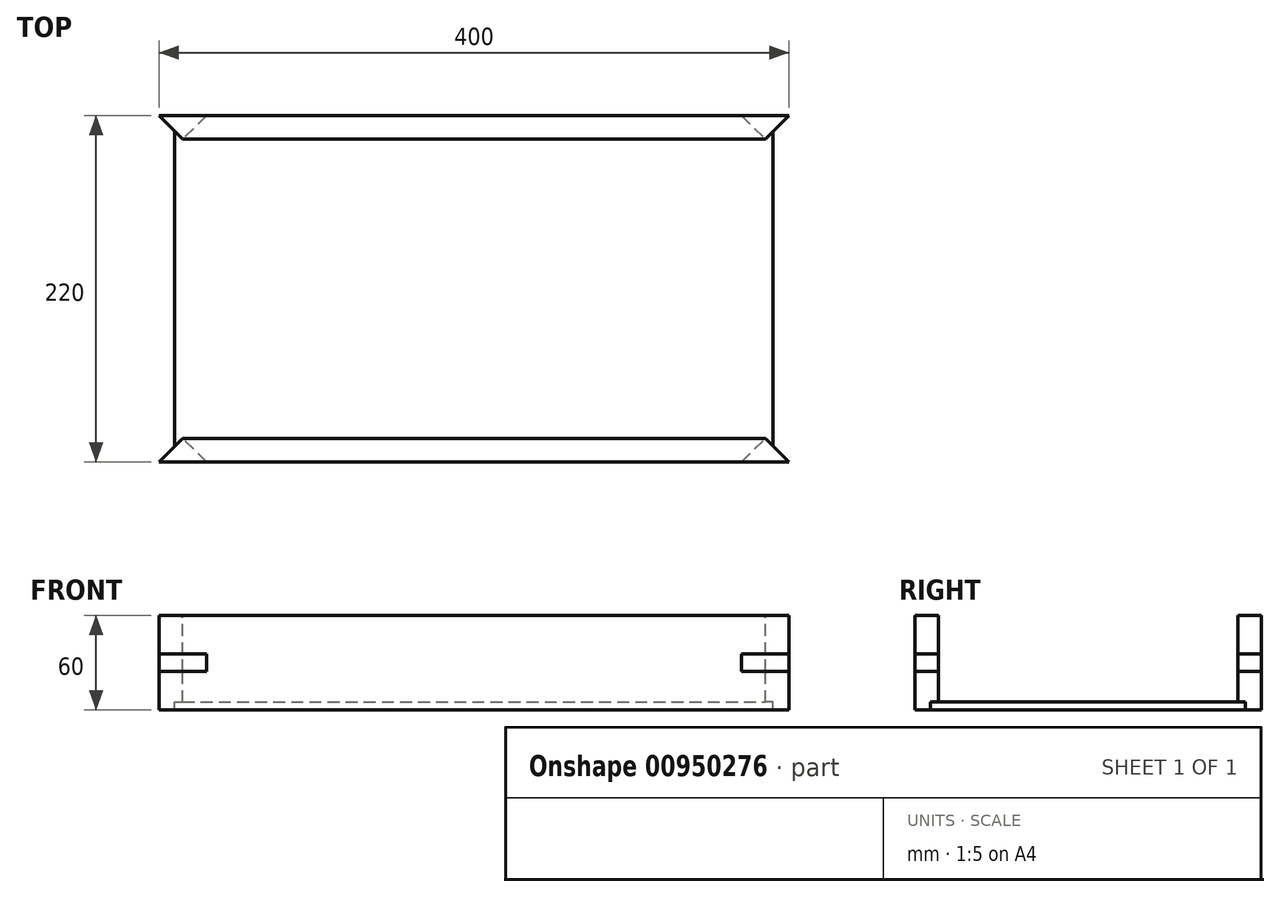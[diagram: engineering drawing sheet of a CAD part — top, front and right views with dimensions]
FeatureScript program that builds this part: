
annotation { "Feature Type Name" : "Feature", "Feature Type Description" : "" }
export const myFeature = defineFeature(function(context is Context, id is Id, definition is map)
    precondition{}
    {
        {
            var Q0;
            Q0=qCreatedBy(makeId("Front.planeOp"),FACE);
            var sketch = newSketch(context, id + "F0", { "sketchPlane" : qUnion([Q0])});
            skLineSegment(sketch, "E0.bottom", {"start": v(200, -30) * mm, "end": v(-200, -30) * mm});
            skLineSegment(sketch, "E0.top", {"start": v(200, 30) * mm, "end": v(-200, 30) * mm});
            skLineSegment(sketch, "E0.left", {"start": v(200, -30) * mm, "end": v(200, 30) * mm});
            skLineSegment(sketch, "E0.right", {"start": v(-200, -30) * mm, "end": v(-200, 30) * mm});
            skPoint(sketch, "E0.middle", {"position": v(0, 0) * mm});
            skSolve(sketch);
        }
        {
            var Q0;
            Q0=makeQuery(id+"F0.imprint","IMPRINT",FACE,{"disambiguationData":[TD([[makeQuery(id+"F0.imprint","IMPRINT",EDGE,{"derivedFrom":sQuery(id+"F0.wireOp",EDGE,"E0.bottom")}),-1.0]])]});
            extrude(context, id + "F1", {"entities" : qUnion([Q0]), "endBound" : BoundingType.SYMMETRIC, "depth" : 15 * mm, "offsetDistance" : 25 * mm});
        }
        {
            var Q0;
            Q0=makeQuery(id+"F1.opExtrude","SWEPT_FACE",FACE,{"disambiguationData":[OSD([sQuery(id+"F0.wireOp",EDGE,"E0.top")])]});
            var sketch = newSketch(context, id + "F2", { "sketchPlane" : qUnion([Q0])});
            skLineSegment(sketch, "E1", {"start": v(200, -7.5) * mm, "end": v(200, 7.5) * mm});
            skLineSegment(sketch, "E2", {"start": v(200, 7.5) * mm, "end": v(185, 7.5) * mm});
            skLineSegment(sketch, "E3", {"start": v(185, 7.5) * mm, "end": v(200, -7.5) * mm});
            skLineSegment(sketch, "E4", {"start": v(-200, -7.5) * mm, "end": v(-200, 7.5) * mm});
            skLineSegment(sketch, "E5", {"start": v(-200, 7.5) * mm, "end": v(-185, 7.5) * mm});
            skLineSegment(sketch, "E6", {"start": v(-185, 7.5) * mm, "end": v(-200, -7.5) * mm});
            skSolve(sketch);
        }
        {
            var Q0;
            Q0=makeQuery(id+"F2.imprint","IMPRINT",FACE,{"disambiguationData":[TD([[makeQuery(id+"F2.imprint","IMPRINT",EDGE,{"derivedFrom":sQuery(id+"F2.wireOp",EDGE,"E4")}),-1.0]])]});
            var Q1;
            Q1=makeQuery(id+"F2.imprint","IMPRINT",FACE,{"disambiguationData":[TD([[makeQuery(id+"F2.imprint","IMPRINT",EDGE,{"derivedFrom":sQuery(id+"F2.wireOp",EDGE,"E1")}),1.0]])]});
            extrude(context, id + "F3", {"entities" : qUnion([Q0, Q1]), "operationType" : NewBodyOperationType.REMOVE, "oppositeDirection" : true, "depth" : 60 * mm, "offsetDistance" : 25 * mm});
        }
        {
            var Q0;
            Q0=makeQuery(id+"F3.boolean.opBoolean","COPY",FACE,{"derivedFrom":makeQuery(id+"F3.opExtrude","SWEPT_FACE",FACE,{"disambiguationData":[OSD([sQuery(id+"F2.wireOp",EDGE,"E3")])]})});
            var sketch = newSketch(context, id + "F4", { "sketchPlane" : qUnion([Q0])});
            skLineSegment(sketch, "E7.bottom", {"start": v(-125.51, -5) * mm, "end": v(-146.72, -5) * mm});
            skLineSegment(sketch, "E7.top", {"start": v(-125.51, 5) * mm, "end": v(-146.72, 5) * mm});
            skLineSegment(sketch, "E7.left", {"start": v(-125.51, -5) * mm, "end": v(-125.51, 5) * mm});
            skLineSegment(sketch, "E7.right", {"start": v(-146.72, -5) * mm, "end": v(-146.72, 5) * mm});
            skPoint(sketch, "E7.middle", {"position": v(-136.12, 0) * mm});
            skSolve(sketch);
        }
        {
            var Q0;
            Q0=makeQuery(id+"F4.imprint","IMPRINT",FACE,{"disambiguationData":[TD([[makeQuery(id+"F4.imprint","IMPRINT",EDGE,{"derivedFrom":sQuery(id+"F4.wireOp",EDGE,"E7.bottom")}),-1.0]])]});
            extrude(context, id + "F5", {"entities" : qUnion([Q0]), "operationType" : NewBodyOperationType.REMOVE, "oppositeDirection" : true, "depth" : 25 * mm, "offsetDistance" : 25 * mm});
        }
        {
            var Q0;
            Q0=makeQuery(id+"F3.boolean.opBoolean","COPY",FACE,{"derivedFrom":makeQuery(id+"F3.opExtrude","SWEPT_FACE",FACE,{"disambiguationData":[OSD([sQuery(id+"F2.wireOp",EDGE,"E6")])]})});
            var sketch = newSketch(context, id + "F6", { "sketchPlane" : qUnion([Q0])});
            skLineSegment(sketch, "E8.bottom", {"start": v(146.72, -5.45) * mm, "end": v(125.51, -5.45) * mm});
            skLineSegment(sketch, "E8.top", {"start": v(146.72, 5.45) * mm, "end": v(125.51, 5.45) * mm});
            skLineSegment(sketch, "E8.left", {"start": v(146.72, -5.45) * mm, "end": v(146.72, 5.45) * mm});
            skLineSegment(sketch, "E8.right", {"start": v(125.51, -5.45) * mm, "end": v(125.51, 5.45) * mm});
            skPoint(sketch, "E8.middle", {"position": v(136.12, 0) * mm});
            skSolve(sketch);
        }
        {
            var Q0;
            Q0=makeQuery(id+"F6.imprint","IMPRINT",FACE,{"disambiguationData":[TD([[makeQuery(id+"F6.imprint","IMPRINT",EDGE,{"derivedFrom":sQuery(id+"F6.wireOp",EDGE,"E8.bottom")}),-1.0]])]});
            extrude(context, id + "F7", {"entities" : qUnion([Q0]), "operationType" : NewBodyOperationType.REMOVE, "oppositeDirection" : true, "depth" : 25 * mm, "offsetDistance" : 25 * mm});
        }
        {
            var Q0;
            Q0=makeQuery(id+"F1.opExtrude","CAP_FACE",FACE,{"disambiguationData":[OSD([sQuery(id+"F0.wireOp",EDGE,"E0.bottom"),sQuery(id+"F0.wireOp",EDGE,"E0.top"),sQuery(id+"F0.wireOp",EDGE,"E0.left"),sQuery(id+"F0.wireOp",EDGE,"E0.right")])],"isStart":false});
            var sketch = newSketch(context, id + "F8", { "sketchPlane" : qUnion([Q0])});
            skLineSegment(sketch, "E9.bottom", {"start": v(160, -25) * mm, "end": v(-160, -25) * mm});
            skLineSegment(sketch, "E9.top", {"start": v(160, 25) * mm, "end": v(-160, 25) * mm});
            skLineSegment(sketch, "E9.left", {"start": v(160, -25) * mm, "end": v(160, 25) * mm});
            skLineSegment(sketch, "E9.right", {"start": v(-160, -25) * mm, "end": v(-160, 25) * mm});
            skPoint(sketch, "E9.middle", {"position": v(0, 0) * mm});
            skSolve(sketch);
        }
        {
            var Q0;
            Q0=makeQuery(id+"F8.imprint","IMPRINT",FACE,{"disambiguationData":[TD([[makeQuery(id+"F8.imprint","IMPRINT",EDGE,{"derivedFrom":sQuery(id+"F8.wireOp",EDGE,"E9.bottom")}),-1.0]])]});
            extrude(context, id + "F9", {"entities" : qUnion([Q0]), "operationType" : NewBodyOperationType.REMOVE, "oppositeDirection" : true, "depth" : 25 * mm, "offsetDistance" : 25 * mm});
        }
        {
            var Q0;
            Q0=makeQuery(id+"F1.opExtrude","CAP_FACE",FACE,{"disambiguationData":[OSD([sQuery(id+"F0.wireOp",EDGE,"E0.bottom"),sQuery(id+"F0.wireOp",EDGE,"E0.top"),sQuery(id+"F0.wireOp",EDGE,"E0.left"),sQuery(id+"F0.wireOp",EDGE,"E0.right")])],"isStart":true});
            var sketch = newSketch(context, id + "F10", { "sketchPlane" : qUnion([Q0])});
            skLineSegment(sketch, "E10.bottom", {"start": v(-160, -25) * mm, "end": v(160, -25) * mm});
            skLineSegment(sketch, "E10.top", {"start": v(-160, -30) * mm, "end": v(160, -30) * mm});
            skLineSegment(sketch, "E10.left", {"start": v(-160, -25) * mm, "end": v(-160, -30) * mm});
            skLineSegment(sketch, "E10.right", {"start": v(160, -25) * mm, "end": v(160, -30) * mm});
            skSolve(sketch);
        }
        {
            var Q0;
            Q0=makeQuery(id+"F10.imprint","IMPRINT",FACE,{"disambiguationData":[TD([[makeQuery(id+"F10.imprint","IMPRINT",EDGE,{"derivedFrom":sQuery(id+"F10.wireOp",EDGE,"E10.bottom")}),-1.0]])]});
            extrude(context, id + "F11", {"entities" : qUnion([Q0]), "operationType" : NewBodyOperationType.REMOVE, "oppositeDirection" : true, "depth" : 5 * mm, "offsetDistance" : 25 * mm});
        }
        {
            var Q0;
            Q0=makeQuery(id+"F11.boolean.opBoolean","MERGE",FACE,{"derivedFrom":[makeQuery(id+"F9.boolean.opBoolean","COPY",FACE,{"derivedFrom":makeQuery(id+"F9.opExtrude","SWEPT_FACE",FACE,{"disambiguationData":[OSD([sQuery(id+"F8.wireOp",EDGE,"E9.right")])]})})],"fromTools":[makeQuery(id+"F11.opExtrude","SWEPT_FACE",FACE,{"disambiguationData":[OSD([sQuery(id+"F10.wireOp",EDGE,"E10.right")])]})]});
            var sketch = newSketch(context, id + "F12", { "sketchPlane" : qUnion([Q0])});
            skLineSegment(sketch, "E11.bottom", {"start": v(7.5, -30) * mm, "end": v(2.5, -30) * mm});
            skLineSegment(sketch, "E11.top", {"start": v(7.5, -25) * mm, "end": v(2.5, -25) * mm});
            skLineSegment(sketch, "E11.left", {"start": v(7.5, -30) * mm, "end": v(7.5, -25) * mm});
            skLineSegment(sketch, "E11.right", {"start": v(2.5, -30) * mm, "end": v(2.5, -25) * mm});
            skSolve(sketch);
        }
        {
            var Q0;
            Q0=makeQuery(id+"F12.imprint","IMPRINT",FACE,{"disambiguationData":[TD([[makeQuery(id+"F12.imprint","IMPRINT",EDGE,{"derivedFrom":sQuery(id+"F12.wireOp",EDGE,"E11.bottom")}),1.0]])]});
            extrude(context, id + "F13", {"entities" : qUnion([Q0]), "operationType" : NewBodyOperationType.REMOVE, "oppositeDirection" : true, "depth" : 50 * mm, "offsetDistance" : 25 * mm});
        }
        {
            var Q0;
            Q0=makeQuery(id+"F1.opExtrude","SWEPT_BODY",BODY,{"disambiguationData":[OSD([sQuery(id+"F0.wireOp",EDGE,"E0.bottom"),sQuery(id+"F0.wireOp",EDGE,"E0.top"),sQuery(id+"F0.wireOp",EDGE,"E0.left"),sQuery(id+"F0.wireOp",EDGE,"E0.right")])]});
            var Q1;
            Q1=qCreatedBy(makeId("Right.planeOp"),FACE);
            mirror(context, id + "F14", {"operationType" : NewBodyOperationType.INTERSECT, "entities" : qUnion([Q0]), "mirrorPlane" : qUnion([Q1])});
        }
        {
            var Q0;
            {var subQ0=makeQuery(id+"F13.boolean.opBoolean","MERGE",FACE,{"derivedFrom":[makeQuery(id+"F11.boolean.opBoolean","COPY",FACE,{"derivedFrom":makeQuery(id+"F11.opExtrude","CAP_FACE",FACE,{"disambiguationData":[OSD([sQuery(id+"F10.wireOp",EDGE,"E10.bottom"),sQuery(id+"F10.wireOp",EDGE,"E10.top"),sQuery(id+"F10.wireOp",EDGE,"E10.left"),sQuery(id+"F10.wireOp",EDGE,"E10.right")])],"isStart":false})})],"fromTools":[makeQuery(id+"F13.opExtrude","SWEPT_FACE",FACE,{"disambiguationData":[OSD([sQuery(id+"F12.wireOp",EDGE,"E11.right")])]})]});Q0=makeQuery(id+"F14.boolean.opBoolean","MERGE",FACE,{"derivedFrom":[subQ0],"fromTools":[makeQuery(id+"F14.boolean.toolComplement.opBoolean","COPY",FACE,{"derivedFrom":makeQuery(id+"F14.opPattern","COPY",FACE,{"derivedFrom":subQ0,"instanceName":"1"})})]});}
            extrude(context, id + "F15", {"entities" : qUnion([Q0]), "depth" : 100 * mm, "offsetDistance" : 25 * mm});
        }
        {
            var Q0;
            Q0=makeQuery(id+"F15.opExtrude","CAP_FACE",FACE,{"disambiguationData":[OSD([sQuery(id+"F10.wireOp",EDGE,"E10.bottom"),sQuery(id+"F10.wireOp",EDGE,"E10.top"),sQuery(id+"F10.wireOp",EDGE,"E10.left"),sQuery(id+"F10.wireOp",EDGE,"E10.right"),sQuery(id+"F12.wireOp",EDGE,"E11.right")])],"isStart":false});
            cPlane(context, id + "F16", {"entities" : qUnion([Q0]), "cplaneType" : CPlaneType.OFFSET, "offset" : 0 * mm, "width" : 150 * mm, "height" : 150 * mm});
        }
        {
            var Q0;
            Q0=makeQuery(id+"F14.boolean.opBoolean","MERGE",FACE,{"derivedFrom":[makeQuery(id+"F5.boolean.opBoolean","COPY",FACE,{"derivedFrom":makeQuery(id+"F5.opExtrude","SWEPT_FACE",FACE,{"disambiguationData":[OSD([sQuery(id+"F4.wireOp",EDGE,"E7.left")])]})})],"fromTools":[makeQuery(id+"F14.boolean.toolComplement.opBoolean","COPY",FACE,{"derivedFrom":makeQuery(id+"F14.opPattern","COPY",FACE,{"derivedFrom":makeQuery(id+"F7.boolean.opBoolean","COPY",FACE,{"derivedFrom":makeQuery(id+"F7.opExtrude","SWEPT_FACE",FACE,{"disambiguationData":[OSD([sQuery(id+"F6.wireOp",EDGE,"E8.right")])]})}),"instanceName":"1"})})]});
            extrude(context, id + "F17", {"entities" : qUnion([Q0]), "depth" : 25 * mm, "offsetDistance" : 25 * mm});
        }
        {
            var Q0;
            Q0=makeQuery(id+"F17.opExtrude","SWEPT_FACE",FACE,{"disambiguationData":[OSD([sQuery(id+"F0.wireOp",EDGE,"E0.top"),sQuery(id+"F2.wireOp",EDGE,"E5"),sQuery(id+"F2.wireOp",EDGE,"E6"),sQuery(id+"F6.wireOp",EDGE,"E8.top"),sQuery(id+"F6.wireOp",EDGE,"E8.right")])]});
            var sketch = newSketch(context, id + "F18", { "sketchPlane" : qUnion([Q0])});
            skLineSegment(sketch, "E12", {"start": v(170, -7.5) * mm, "end": v(200, -7.5) * mm});
            skLineSegment(sketch, "E13", {"start": v(200, -7.5) * mm, "end": v(202.68, -10.18) * mm});
            skLineSegment(sketch, "E14", {"start": v(202.68, -10.18) * mm, "end": v(187.68, -25.18) * mm});
            skLineSegment(sketch, "E15", {"start": v(187.68, -25.18) * mm, "end": v(170, -7.5) * mm});
            skSolve(sketch);
        }
        {
            var Q0;
            Q0=makeQuery(id+"F18.imprint","IMPRINT",FACE,{"disambiguationData":[TD([[makeQuery(id+"F18.imprint","IMPRINT",EDGE,{"derivedFrom":sQuery(id+"F18.wireOp",EDGE,"E12")}),-1.0]])]});
            extrude(context, id + "F19", {"entities" : qUnion([Q0]), "operationType" : NewBodyOperationType.REMOVE, "oppositeDirection" : true, "depth" : 25 * mm, "offsetDistance" : 25 * mm});
        }
        {
            var Q0;
            Q0=makeQuery(id+"F15.opExtrude","SWEPT_BODY",BODY,{"disambiguationData":[OSD([sQuery(id+"F10.wireOp",EDGE,"E10.bottom"),sQuery(id+"F10.wireOp",EDGE,"E10.top"),sQuery(id+"F10.wireOp",EDGE,"E10.left"),sQuery(id+"F10.wireOp",EDGE,"E10.right"),sQuery(id+"F12.wireOp",EDGE,"E11.right")])]});
            var Q1;
            Q1=qCreatedBy(id+"F16.planeOp",FACE);
            mirror(context, id + "F20", {"operationType" : NewBodyOperationType.ADD, "entities" : qUnion([Q0]), "mirrorPlane" : qUnion([Q1])});
        }
        {
            var Q0;
            Q0=makeQuery(id+"F17.opExtrude","SWEPT_BODY",BODY,{"disambiguationData":[OSD([sQuery(id+"F4.wireOp",EDGE,"E7.left"),sQuery(id+"F6.wireOp",EDGE,"E8.right")])]});
            var Q1;
            Q1=qCreatedBy(makeId("Right.planeOp"),FACE);
            mirror(context, id + "F21", {"entities" : qUnion([Q0]), "mirrorPlane" : qUnion([Q1])});
        }
        {
            var Q0;
            Q0=makeQuery(id+"F1.opExtrude","SWEPT_BODY",BODY,{"disambiguationData":[OSD([sQuery(id+"F0.wireOp",EDGE,"E0.bottom"),sQuery(id+"F0.wireOp",EDGE,"E0.top"),sQuery(id+"F0.wireOp",EDGE,"E0.left"),sQuery(id+"F0.wireOp",EDGE,"E0.right")])]});
            var Q1;
            Q1=makeQuery(id+"F21.opPattern","COPY",BODY,{"derivedFrom":makeQuery(id+"F17.opExtrude","SWEPT_BODY",BODY,{"disambiguationData":[OSD([sQuery(id+"F4.wireOp",EDGE,"E7.left"),sQuery(id+"F6.wireOp",EDGE,"E8.right")])]}),"instanceName":"1"});
            var Q2;
            Q2=makeQuery(id+"F17.opExtrude","SWEPT_BODY",BODY,{"disambiguationData":[OSD([sQuery(id+"F4.wireOp",EDGE,"E7.left"),sQuery(id+"F6.wireOp",EDGE,"E8.right")])]});
            var Q3;
            Q3=qCreatedBy(id+"F16.planeOp",FACE);
            mirror(context, id + "F22", {"entities" : qUnion([Q0, Q1, Q2]), "mirrorPlane" : qUnion([Q3])});
        }
        {
            var Q0;
            Q0=makeQuery(id+"F22.opPattern","COPY",FACE,{"derivedFrom":makeQuery(id+"F9.boolean.opBoolean","COPY",FACE,{"derivedFrom":makeQuery(id+"F9.opExtrude","SWEPT_FACE",FACE,{"disambiguationData":[OSD([sQuery(id+"F8.wireOp",EDGE,"E9.top")])]})}),"instanceName":"1"});
            extrude(context, id + "F23", {"entities" : qUnion([Q0]), "operationType" : NewBodyOperationType.ADD, "depth" : 50 * mm, "offsetDistance" : 25 * mm});
        }
        {
            var Q0;
            Q0=makeQuery(id+"F9.boolean.opBoolean","COPY",FACE,{"derivedFrom":makeQuery(id+"F9.opExtrude","SWEPT_FACE",FACE,{"disambiguationData":[OSD([sQuery(id+"F8.wireOp",EDGE,"E9.top")])]})});
            extrude(context, id + "F24", {"entities" : qUnion([Q0]), "operationType" : NewBodyOperationType.ADD, "depth" : 50 * mm, "offsetDistance" : 25 * mm});
        }
    });
